# Revit family: Zumtobel LF3-E M625L
name_source: partatom
category: Leuchten
revit_build: Autodesk Revit 2016 (Build: 20150714_1515(x64)
units: mm (PartAtom-declared; Revit-internal decimal feet)

## family parameters
Basisbauteil = Decke
Beim Laden mit Abzugskörper schneiden = Nein
Bemaßung runder Anschluss = Durchmesser verwenden
Gemeinsam genutzt = Nein
Immer vertikal = Ja
Lichtquelle = Ja
OmniClass-Nummer = 23.80.70.11
OmniClass-Titel = Luminaries for Internal Lighting
Raumberechnungspunkt = Nein
Teiletyp = Normal

## types (1)
- LF3 E 5000LED M625L
    Baugruppenkennzeichen = D5020200
    Beschreibung = Recessed micro-pyramidal optic LED luminaire
    Datei für fotometrisches Netz = D41758AA_LF3_E_5000-940_M625L12_LDE_KA_WH.IES
    Emissionsform beim Rendern sichtbar = Ja
    Farbfilter = 16777215
    Farbtemperaturverschiebung bei Dämpfen der Lampe = <Keine Auswahl>
    Height = 90 mm  [stored 0.295276 ft]
    Hersteller = Zumtobel Lighting
    Lampe = LED
    Length = 300 mm
    Modell = 42186934
    Neigungswinkel = 90.00°
    Scheinlast = 37 VA
    URL = http://www.zumtobel.com
    Von Breite des Rechtecks ausssenden = 1226 mm  [stored 4.02231 ft]
    Von Länge des Rechtecks aussenden = 278 mm  [stored 0.912073 ft]
    Width = 1248 mm  [stored 4.09449 ft]

note: [stored X ft] marks values corroborated as IEEE doubles in the binary element streams (Revit-internal decimal feet)

## geometry (parser evidence)
native form markers: Sweep x5
no freeform markers — native parametric forms only
